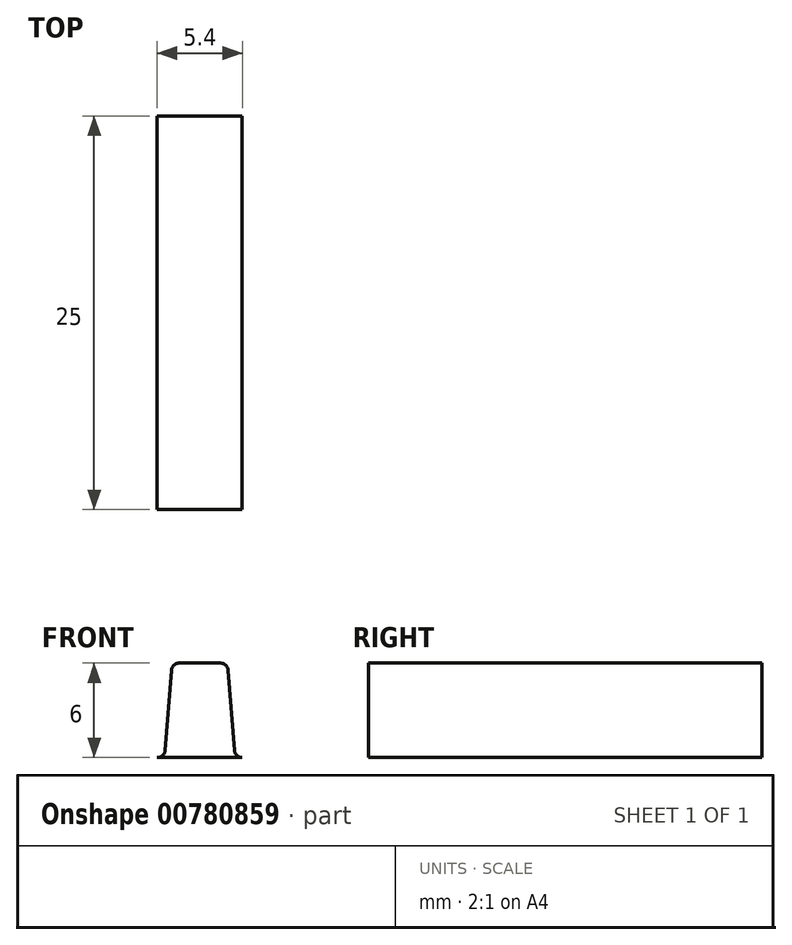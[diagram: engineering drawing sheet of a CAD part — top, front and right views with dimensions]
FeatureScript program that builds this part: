
annotation { "Feature Type Name" : "Feature", "Feature Type Description" : "" }
export const myFeature = defineFeature(function(context is Context, id is Id, definition is map)
    precondition{}
    {
        {
            var Q0;
            Q0=qCreatedBy(makeId("Front.planeOp"),FACE);
            var sketch = newSketch(context, id + "F0", { "sketchPlane" : qUnion([Q0])});
            skArc(sketch, "E0", {"start": v(0, 0) * mm, "mid": v(0.34, 0.13) * mm, "end": v(0.5, 0.46) * mm});
            skLineSegment(sketch, "E1", {"start": v(0.5, 0.46) * mm, "end": v(0.9, 5.54) * mm});
            skLineSegment(sketch, "E2", {"start": v(1.4, 6) * mm, "end": v(4, 6) * mm});
            skLineSegment(sketch, "E3", {"start": v(4.5, 5.54) * mm, "end": v(4.9, 0.46) * mm});
            skArc(sketch, "E4", {"start": v(1.4, 6) * mm, "mid": v(1.06, 5.87) * mm, "end": v(0.9, 5.54) * mm});
            skArc(sketch, "E5", {"start": v(4.9, 0.46) * mm, "mid": v(5.06, 0.13) * mm, "end": v(5.4, 0) * mm});
            skLineSegment(sketch, "E6", {"start": v(5.4, 0) * mm, "end": v(7.43, 0) * mm, "construction": true});
            skLineSegment(sketch, "E7", {"start": v(0, 0) * mm, "end": v(5.4, 0) * mm});
            skArc(sketch, "E8", {"start": v(4.5, 5.54) * mm, "mid": v(4.34, 5.87) * mm, "end": v(4, 6) * mm});
            skLineSegment(sketch, "E9", {"start": v(2.7, 6) * mm, "end": v(2.7, 0) * mm, "construction": true});
            skLineSegment(sketch, "E10", {"start": v(2.7, 3) * mm, "end": v(4.7, 3) * mm, "construction": true});
            skLineSegment(sketch, "E11", {"start": v(2.7, 3) * mm, "end": v(0.7, 3) * mm, "construction": true});
            skSolve(sketch);
        }
        {
            var Q0;
            Q0 = qSketchRegion(id + "F0", true);
            extrude(context, id + "F1", {"entities" : qUnion([Q0]), "depth" : 25 * mm, "offsetDistance" : 25 * mm});
        }
    });
